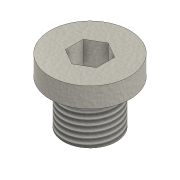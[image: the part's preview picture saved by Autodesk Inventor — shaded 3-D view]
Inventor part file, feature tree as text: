
AUTODESK INVENTOR PART (.ipt)
format: ipt  version: 2022.3 (Build 263350000, 350)  size: 135,168 bytes
history: native  units: mm
features: extrude x4, sketch x4, other x1, thread x1
ambient origin geometry x8: Origin, YZ Plane, XZ Plane, XY Plane, X Axis, Y Axis, Z Axis, Center Point
bodies: Body1 (feature_tree)
feature tree (10):
  other  "Sólido1"
  extrude  "Extrusión1"  Depth=12.0mm TaperAngle=0.0deg
  extrude  "Extrusión2"  Depth=5.5mm TaperAngle=0.0deg
  extrude  "Extrusión3"  Depth=11.4mm TaperAngle=0.0deg
  thread  "Rosca1"  [1 undecoded]
  extrude  "Extrusión4"  Depth=1.0mm TaperAngle=0.0deg
  sketch  "Boceto1"  dims[d0=14.55mm d1=12.0mm d2=0.0mm]
  sketch  "Boceto2"  dims[d3=22.0mm d4=5.5mm d5=0.0mm]
  sketch  "Boceto3"  dims[d6=4.325mm d7=11.4mm d8=0.0mm d9=9.0mm d10=0.0mm]
  sketch  "Boceto4"  dims[d11=20.0mm d12=1.0mm d13=0.0mm]
note: 1 required parameter value undecoded (feature->parameter linkage not recoverable at this tier; creation-order binding heuristic only, values carry confidence <= 0.55)
